# Revit family: Barrier_Gate-Assembly_AutoGate_Shield-M30-Shallow
name_source: partatom
category: Generic Models
revit_build: Autodesk Revit 2015 (Build: 20140606_1530(x64)
units: mm (PartAtom-declared; Revit-internal decimal feet)

## types (1)
- as Specified
    Assembly Code = E1030900
    Construction Details = http://www.arcat.com
    Default Elevation = 0' - 0"
    Description = AutoGate Anti-Ram M30 Shallow Foundation Vertical Pivot Gate - The Shield with Arm Design as Specified
    Electrical_Voltage = 115 V
    Expected Lifespan (Years) = 0
    Has Battery Backup = No
    Keynote = 32 21 00
    Lift Travel Speed = 7 - 14 seconds
    Maintenance Schedule (Months) = 0
    Manufacturer = AutoGate, Inc
    Manufacturer Fax = 419-588-3514
    Manufacturer Website = http://autogate.com
    Model = The Shield M30 Shallow Foundation
    Product Data = http://www.arcat.com
    Revision = R1_2016-11
    Sales Information = http://autogate.com
    Specification = http://www.arcat.com
    Standards Conformance = ASTM F2656 M30/P1  ;  DOS K4/L3
    URL = http://autogate.com
    Unit Depth = 0' - 4"
    Warranty Duration (Years) = 0

## geometry (parser evidence)
native form markers: Blend x8, Sweep x6
no freeform markers — native parametric forms only
